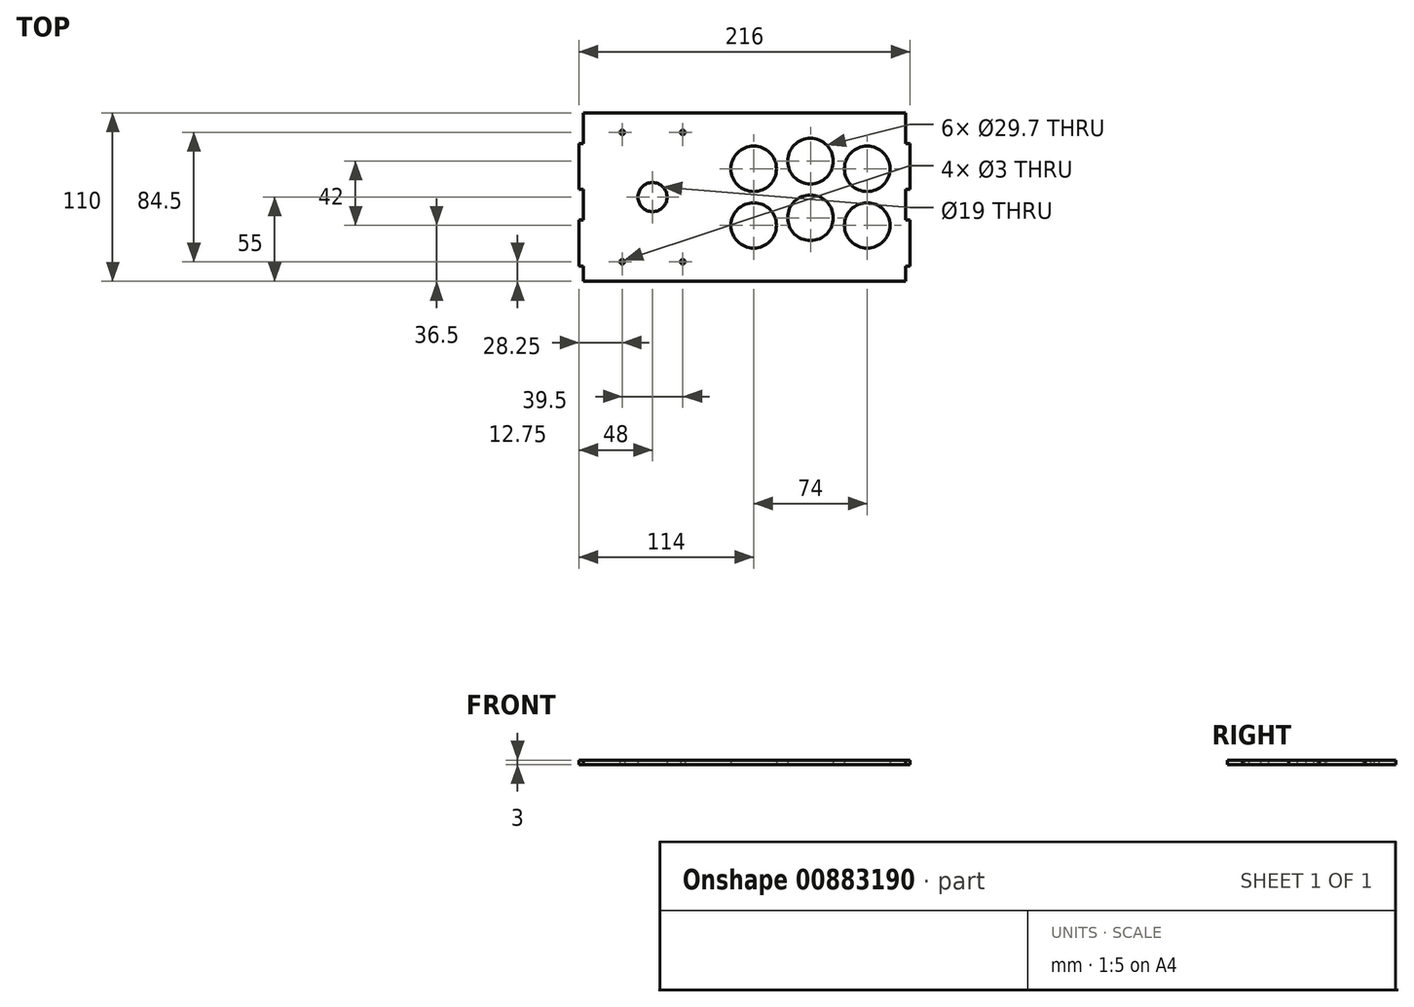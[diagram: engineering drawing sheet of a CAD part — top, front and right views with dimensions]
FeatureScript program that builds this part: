
annotation { "Feature Type Name" : "Feature", "Feature Type Description" : "" }
export const myFeature = defineFeature(function(context is Context, id is Id, definition is map)
    precondition{}
    {
        {
            var Q0;
            Q0=qCreatedBy(makeId("Top.planeOp"),FACE);
            var sketch = newSketch(context, id + "F0", { "sketchPlane" : qUnion([Q0])});
            skLineSegment(sketch, "E0.bottom", {"start": v(-105, 55) * mm, "end": v(105, 55) * mm});
            skLineSegment(sketch, "E0.top", {"start": v(-105, -55) * mm, "end": v(105, -55) * mm});
            skLineSegment(sketch, "E0.left", {"start": v(-105, 55) * mm, "end": v(-105, -55) * mm});
            skLineSegment(sketch, "E0.right", {"start": v(105, 55) * mm, "end": v(105, -55) * mm});
            skPoint(sketch, "E0.middle", {"position": v(0, 0) * mm});
            skCircle(sketch, "E1", {"center": v(6, 18.5) * mm, "radius": 14.85 * mm});
            skCircle(sketch, "E2", {"center": v(43, 23.5) * mm, "radius": 14.85 * mm});
            skCircle(sketch, "E3", {"center": v(80, 18.5) * mm, "radius": 14.85 * mm});
            skCircle(sketch, "E4", {"center": v(6, -18.5) * mm, "radius": 14.85 * mm});
            skCircle(sketch, "E5", {"center": v(43, -13.5) * mm, "radius": 14.85 * mm});
            skCircle(sketch, "E6", {"center": v(80, -18.5) * mm, "radius": 14.85 * mm});
            skCircle(sketch, "E7", {"center": v(-60, 0) * mm, "radius": 9.5 * mm});
            skCircle(sketch, "E8", {"center": v(-79.75, 42.25) * mm, "radius": 1.5 * mm});
            skCircle(sketch, "E9.MirrorC", {"center": v(-40.25, 42.25) * mm, "radius": 1.5 * mm});
            skLineSegment(sketch, "E10", {"start": v(-105, 0) * mm, "end": v(105, 0) * mm, "construction": true});
            skCircle(sketch, "E11.MirrorC", {"center": v(-40.25, -42.25) * mm, "radius": 1.5 * mm});
            skCircle(sketch, "E12.MirrorC", {"center": v(-79.75, -42.25) * mm, "radius": 1.5 * mm});
            skLineSegment(sketch, "E13", {"start": v(6, 18.5) * mm, "end": v(6, -18.5) * mm, "construction": true});
            skPoint(sketch, "E14", {"position": v(6, 0) * mm});
            skLineSegment(sketch, "E15", {"start": v(105, -45) * mm, "end": v(108, -45) * mm});
            skLineSegment(sketch, "E16", {"start": v(108, -45) * mm, "end": v(108, -15) * mm});
            skLineSegment(sketch, "E17", {"start": v(108, -15) * mm, "end": v(105, -15) * mm});
            skLineSegment(sketch, "E18", {"start": v(105, 35) * mm, "end": v(108, 35) * mm});
            skLineSegment(sketch, "E19", {"start": v(108, 35) * mm, "end": v(108, 5) * mm});
            skLineSegment(sketch, "E20", {"start": v(108, 5) * mm, "end": v(105, 5) * mm});
            skLineSegment(sketch, "E21", {"start": v(0, 55) * mm, "end": v(0, -55) * mm, "construction": true});
            skLineSegment(sketch, "E22.MirrorCS", {"start": v(-105, 35) * mm, "end": v(-108, 35) * mm});
            skLineSegment(sketch, "E23.MirrorCS", {"start": v(-108, 35) * mm, "end": v(-108, 5) * mm});
            skLineSegment(sketch, "E24.MirrorCS", {"start": v(-108, 5) * mm, "end": v(-105, 5) * mm});
            skLineSegment(sketch, "E25.MirrorCS", {"start": v(-108, -15) * mm, "end": v(-105, -15) * mm});
            skLineSegment(sketch, "E26.MirrorCS", {"start": v(-108, -45) * mm, "end": v(-108, -15) * mm});
            skLineSegment(sketch, "E27.MirrorCS", {"start": v(-105, -45) * mm, "end": v(-108, -45) * mm});
            skLineSegment(sketch, "E28", {"start": v(-79.75, 42.25) * mm, "end": v(-40.25, 42.25) * mm, "construction": true});
            skPoint(sketch, "E29", {"position": v(-60, 42.25) * mm});
            skLineSegment(sketch, "E30", {"start": v(-40.25, -42.25) * mm, "end": v(-40.25, 42.25) * mm, "construction": true});
            skPoint(sketch, "E31", {"position": v(-40.25, 0) * mm});
            skSolve(sketch);
        }
        {
            var Q0;
            Q0 = qSketchRegion(id + "F0", true);
            extrude(context, id + "F1", {"entities" : qUnion([Q0]), "depth" : 3 * mm, "offsetDistance" : 25 * mm});
        }
    });
